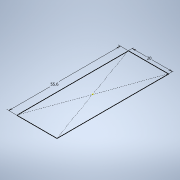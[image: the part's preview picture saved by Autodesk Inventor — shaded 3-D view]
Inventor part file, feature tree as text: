
AUTODESK INVENTOR PART (.ipt)
format: ipt  version: 2022 (Build 260153000, 153)  size: 95,232 bytes
history: native  units: in
note: dims shown in document units (in); Inventor stores cm internally (conversion verified against a paired STEP export)
features: sketch x1
ambient origin geometry x8: Origin, YZ Plane, XZ Plane, XY Plane, X Axis, Y Axis, Z Axis, Center Point
feature tree (1):
  sketch  "Sketch1"  dims[d0=2.189in d1=0.7874in]
